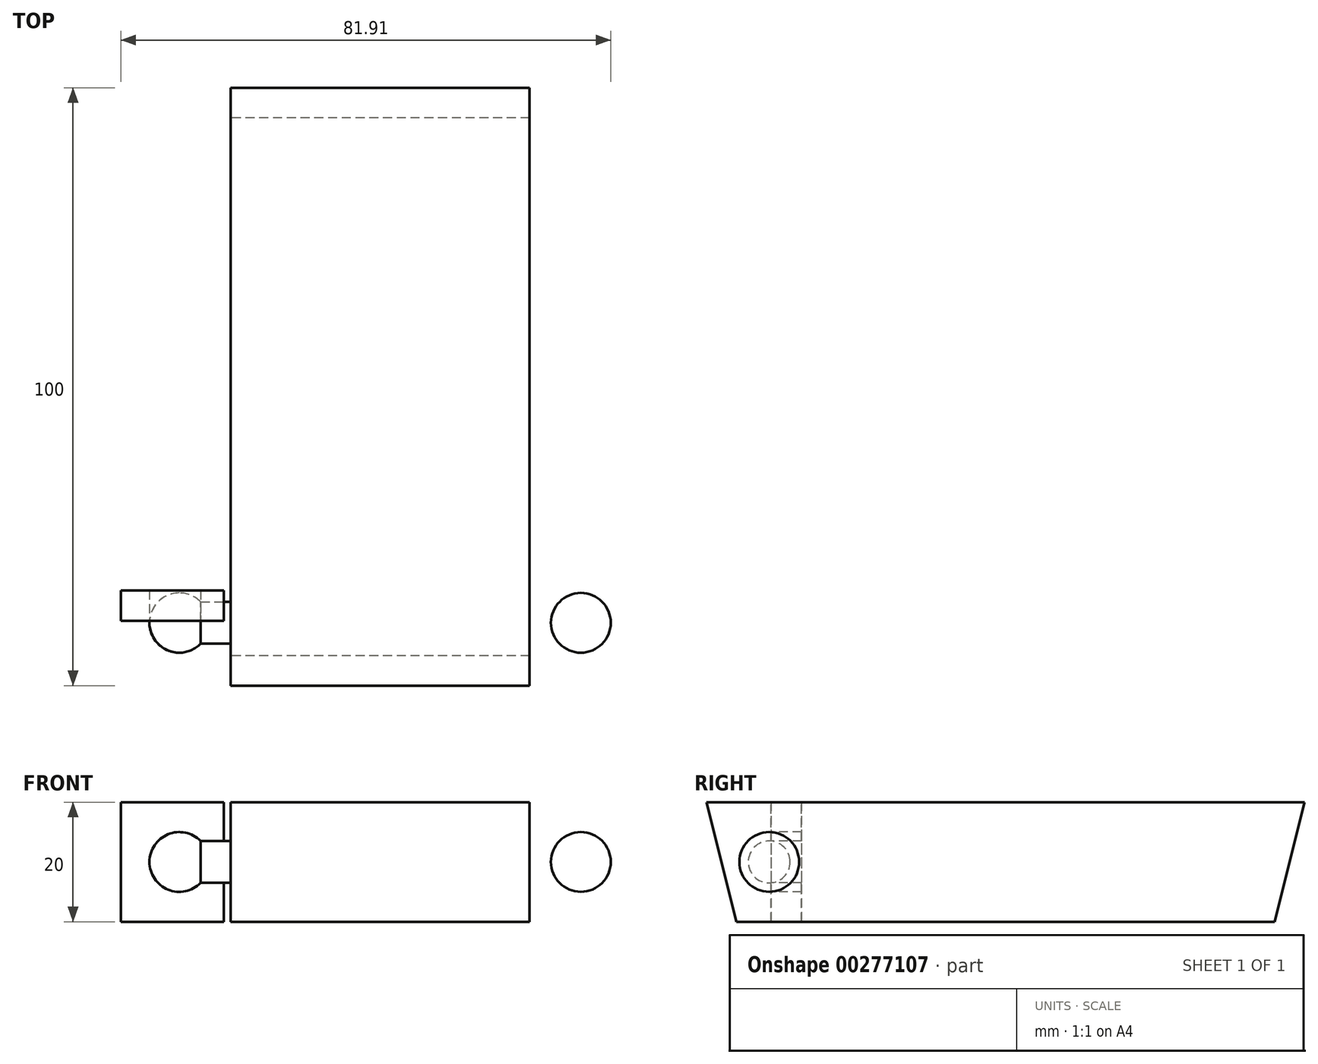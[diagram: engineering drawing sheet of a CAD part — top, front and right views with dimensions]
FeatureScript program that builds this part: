
annotation { "Feature Type Name" : "Feature", "Feature Type Description" : "" }
export const myFeature = defineFeature(function(context is Context, id is Id, definition is map)
    precondition{}
    {
        {
            var Q0;
            Q0=qCreatedBy(makeId("Top.planeOp"),FACE);
            var sketch = newSketch(context, id + "F0", { "sketchPlane" : qUnion([Q0])});
            skLineSegment(sketch, "E0.bottom", {"start": v(25, 50) * mm, "end": v(-25, 50) * mm});
            skLineSegment(sketch, "E0.top", {"start": v(25, -50) * mm, "end": v(-25, -50) * mm});
            skLineSegment(sketch, "E0.left", {"start": v(25, 50) * mm, "end": v(25, -50) * mm});
            skLineSegment(sketch, "E0.right", {"start": v(-25, 50) * mm, "end": v(-25, -50) * mm});
            skPoint(sketch, "E0.middle", {"position": v(0, 0) * mm});
            skSolve(sketch);
        }
        {
            var Q0;
            Q0=qCreatedBy(makeId("Top.planeOp"),FACE);
            cPlane(context, id + "F1", {"entities" : qUnion([Q0]), "cplaneType" : CPlaneType.OFFSET, "offset" : 20 * mm, "oppositeDirection" : true, "width" : 150 * mm, "height" : 150 * mm});
        }
        {
            var Q0;
            Q0=qCreatedBy(id+"F1.planeOp",FACE);
            var sketch = newSketch(context, id + "F2", { "sketchPlane" : qUnion([Q0])});
            skLineSegment(sketch, "E1.bottom", {"start": v(25, -45) * mm, "end": v(-25, -45) * mm});
            skLineSegment(sketch, "E1.top", {"start": v(25, 45) * mm, "end": v(-25, 45) * mm});
            skLineSegment(sketch, "E1.left", {"start": v(25, -45) * mm, "end": v(25, 45) * mm});
            skLineSegment(sketch, "E1.right", {"start": v(-25, -45) * mm, "end": v(-25, 45) * mm});
            skPoint(sketch, "E1.middle", {"position": v(0, 0) * mm});
            skSolve(sketch);
        }
        {
            var Q0;
            Q0=makeQuery(id+"F0.imprint","IMPRINT",FACE,{"disambiguationData":[TD([[makeQuery(id+"F0.imprint","IMPRINT",EDGE,{"derivedFrom":sQuery(id+"F0.wireOp",EDGE,"E0.bottom")}),1.0]])]});
            var Q1;
            Q1=makeQuery(id+"F2.imprint","IMPRINT",FACE,{"disambiguationData":[TD([[makeQuery(id+"F2.imprint","IMPRINT",EDGE,{"derivedFrom":sQuery(id+"F2.wireOp",EDGE,"E1.bottom")}),-1.0]])]});
            loft(context, id + "F3", {"sheetProfilesArray" : [{ "sheetProfileEntities" : qUnion([Q0]) }, { "sheetProfileEntities" : qUnion([Q1]) }]});
        }
        {
            var Q0;
            Q0=makeQuery(id+"F3.opLoft","SWEPT_FACE",FACE,{"disambiguationData":[OSD([sQuery(id+"F0.wireOp",EDGE,"E0.bottom"),sQuery(id+"F0.wireOp",EDGE,"E0.top"),sQuery(id+"F0.wireOp",EDGE,"E0.right"),sQuery(id+"F2.wireOp",EDGE,"E1.bottom"),sQuery(id+"F2.wireOp",EDGE,"E1.top"),sQuery(id+"F2.wireOp",EDGE,"E1.right")])]});
            var sketch = newSketch(context, id + "F4", { "sketchPlane" : qUnion([Q0])});
            skCircle(sketch, "E2", {"center": v(39.5, -10) * mm, "radius": 3.5 * mm});
            skPoint(sketch, "E2.centerSnap0", {"position": v(47.5, -10) * mm});
            skLineSegment(sketch, "E3.0.0", {"start": v(-50, 0) * mm, "end": v(-45, -20) * mm, "construction": true});
            skLineSegment(sketch, "E3.0.1", {"start": v(-45, -20) * mm, "end": v(45, -20) * mm, "construction": true});
            skLineSegment(sketch, "E3.0.2", {"start": v(45, -20) * mm, "end": v(50, 0) * mm, "construction": true});
            skLineSegment(sketch, "E3.0.3", {"start": v(50, 0) * mm, "end": v(-50, 0) * mm, "construction": true});
            skLineSegment(sketch, "E4", {"start": v(39.5, -20) * mm, "end": v(39.5, 0) * mm, "construction": true});
            skLineSegment(sketch, "E5", {"start": v(47.5, -10) * mm, "end": v(26.58, -10) * mm, "construction": true});
            skSolve(sketch);
        }
        {
            var Q0;
            Q0=makeQuery(id+"F4.imprint","IMPRINT",FACE,{"disambiguationData":[TD([[makeQuery(id+"F4.imprint","IMPRINT",EDGE,{"derivedFrom":sQuery(id+"F4.wireOp",EDGE,"E2")}),1.0]])]});
            extrude(context, id + "F5", {"entities" : qUnion([Q0]), "depth" : 5 * mm});
        }
        {
            var Q0;
            Q0=sQuery(id+"F4.wireOp",EDGE,"E5");
            cPlane(context, id + "F6", {"entities" : qUnion([Q0]), "cplaneType" : CPlaneType.LINE_ANGLE, "offset" : 25 * mm, "angle" : 0 * degree, "width" : 150 * mm, "height" : 150 * mm});
        }
        {
            var Q0;
            Q0=qCreatedBy(id+"F6.planeOp",FACE);
            var sketch = newSketch(context, id + "F7", { "sketchPlane" : qUnion([Q0])});
            skLineSegment(sketch, "E6.0.0", {"start": v(-30, -43) * mm, "end": v(-30, -36) * mm, "construction": true});
            skLineSegment(sketch, "E7", {"start": v(-30, -39.5) * mm, "end": v(-44.2, -39.5) * mm, "construction": true});
            skArc(sketch, "E8", {"start": v(-33.57, -34.5) * mm, "mid": v(-38.57, -39.5) * mm, "end": v(-33.57, -44.5) * mm});
            skLineSegment(sketch, "E9", {"start": v(-33.57, -44.5) * mm, "end": v(-33.57, -34.5) * mm});
            skSolve(sketch);
        }
        {
            var Q0;
            Q0 = qSketchRegion(id + "F7", true);
            var Q1;
            Q1=sQuery(id+"F7.wireOp",EDGE,"E9");
            revolve(context, id + "F8", {"entities" : qUnion([Q0]), "axis" : qUnion([Q1]), "revolveType" : RevolveType.FULL});
        }
        {
            var Q0;
            Q0=makeQuery(id+"F8.opRevolve","SWEPT_BODY",BODY,{"disambiguationData":[OSD([sQuery(id+"F7.wireOp",EDGE,"E8"),sQuery(id+"F7.wireOp",EDGE,"E9")])]});
            var Q1;
            Q1=qCreatedBy(makeId("Right.planeOp"),FACE);
            mirror(context, id + "F9", {"operationType" : NewBodyOperationType.ADD, "entities" : qUnion([Q0]), "mirrorPlane" : qUnion([Q1])});
        }
        {
            var Q0;
            Q0=qCreatedBy(makeId("Front.planeOp"),FACE);
            cPlane(context, id + "F10", {"entities" : qUnion([Q0]), "cplaneType" : CPlaneType.OFFSET, "offset" : 39.2 * mm, "width" : 150 * mm, "height" : 150 * mm});
        }
        {
            var Q0;
            Q0=qCreatedBy(id+"F10.planeOp",FACE);
            var sketch = newSketch(context, id + "F11", { "sketchPlane" : qUnion([Q0])});
            skArc(sketch, "E10", {"start": v(-30, -6.5) * mm, "mid": v(-38.57, -10) * mm, "end": v(-30, -13.5) * mm});
            skLineSegment(sketch, "E11", {"start": v(-26.12, -13.5) * mm, "end": v(-30, -13.5) * mm});
            skLineSegment(sketch, "E12", {"start": v(-30, -6.5) * mm, "end": v(-26.12, -6.5) * mm});
            skLineSegment(sketch, "E13", {"start": v(-26.12, -6.5) * mm, "end": v(-26.12, -13.5) * mm});
            skLineSegment(sketch, "E14", {"start": v(-26.12, -6.5) * mm, "end": v(-26.12, 0) * mm});
            skLineSegment(sketch, "E15", {"start": v(-26.12, 0) * mm, "end": v(-43.34, 0) * mm});
            skLineSegment(sketch, "E16.0", {"start": v(-25, 0) * mm, "end": v(-25, -20) * mm, "construction": true});
            skLineSegment(sketch, "E17", {"start": v(-43.34, 0) * mm, "end": v(-43.34, -20) * mm});
            skLineSegment(sketch, "E18", {"start": v(-43.34, -20) * mm, "end": v(-26.12, -20) * mm});
            skLineSegment(sketch, "E19", {"start": v(-26.12, -20) * mm, "end": v(-26.12, -13.5) * mm});
            skSolve(sketch);
        }
        {
            var Q0;
            Q0=makeQuery(id+"F11.imprint","IMPRINT",FACE,{"disambiguationData":[TD([[makeQuery(id+"F11.imprint","IMPRINT",EDGE,{"derivedFrom":sQuery(id+"F11.wireOp",EDGE,"E10")}),-1.0]])]});
            extrude(context, id + "F12", {"entities" : qUnion([Q0]), "oppositeDirection" : true, "depth" : 5.1 * mm});
        }
    });
